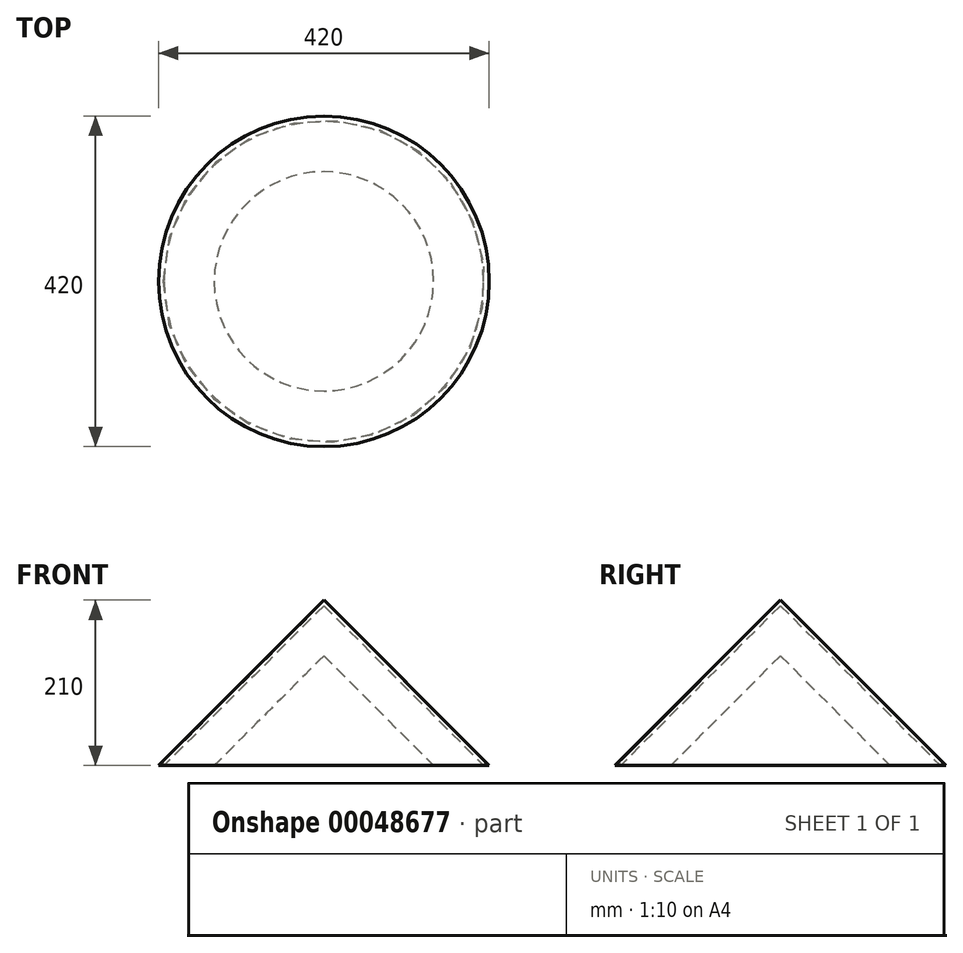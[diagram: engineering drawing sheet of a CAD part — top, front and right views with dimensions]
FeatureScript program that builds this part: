
annotation { "Feature Type Name" : "Feature", "Feature Type Description" : "" }
export const myFeature = defineFeature(function(context is Context, id is Id, definition is map)
    precondition{}
    {
        {
            var Q0;
            Q0=qCreatedBy(makeId("Front.planeOp"),FACE);
            var sketch = newSketch(context, id + "F0", { "sketchPlane" : qUnion([Q0])});
            skLineSegment(sketch, "E0", {"start": v(0, 0) * mm, "end": v(0, 210) * mm});
            skLineSegment(sketch, "E1", {"start": v(0, 210) * mm, "end": v(210, 0) * mm});
            skLineSegment(sketch, "E2", {"start": v(210, 0) * mm, "end": v(0, 0) * mm});
            skSolve(sketch);
        }
        {
            var Q0;
            Q0 = qSketchRegion(id + "F0", true);
            var Q1;
            Q1=sQuery(id+"F0.wireOp",EDGE,"E0");
            revolve(context, id + "F1", {"entities" : qUnion([Q0]), "axis" : qUnion([Q1]), "revolveType" : RevolveType.FULL});
        }
        {
            var Q0;
            Q0=makeQuery(id+"F1.opRevolve","SWEPT_FACE",FACE,{"disambiguationData":[OSD([sQuery(id+"F0.wireOp",EDGE,"E2")])]});
            shell(context, id + "F2", {"entities" : qUnion([Q0]), "thickness" : 5 * mm});
        }
        {
            var Q0;
            Q0=makeQuery(id+"F1.opRevolve","SWEPT_EDGE",EDGE,{"disambiguationData":[OSD([sQuery(id+"F0.wireOp",EDGE,"E1"),sQuery(id+"F0.wireOp",EDGE,"E2")])]});
            fillet(context, id + "F3", {"entities" : qUnion([Q0]), "radius" : 5 * mm, "tangentPropagation" : true, "allowEdgeOverflow" : false});
        }
        {
            var Q0;
            Q0 = qSketchRegion(id + "F0", true);
            var Q1;
            Q1=sQuery(id+"F0.wireOp",EDGE,"E0");
            revolve(context, id + "F4", {"entities" : qUnion([Q0]), "axis" : qUnion([Q1]), "revolveType" : RevolveType.FULL});
        }
        {
            var Q0;
            Q0=makeQuery(id+"F4.opRevolve","SWEPT_FACE",FACE,{"disambiguationData":[OSD([sQuery(id+"F0.wireOp",EDGE,"E2")])]});
            shell(context, id + "F5", {"entities" : qUnion([Q0]), "thickness" : 50 * mm});
        }
    });
